# Revit family: Flopro Z2 Cuadrado
name_source: partatom
category: Luminarias
revit_build: Autodesk Revit 2015 (Build: 20140606_1530(x64)
units: mm (PartAtom-declared; Revit-internal decimal feet)

## types (4) — shared parameters
Anchura rectángulo de emisión = 72 mm  [stored 0.23622 ft]
Cambio de temperatura de color de luz atenuada = <Ninguno>
Fabricante = SECOM ILUMINACIÓN
Filtro de color = 16777215
Forma visible en renderización = No
Longitud de rectángulo de emisión = 72 mm  [stored 0.23622 ft]
Lámpara = LED Osram Duris
Ángulo de inclinación = 90.00°

## per-type parameters (varying)
| type | Archivo de red fotométrica | Comentarios de vataje | Descripción | Modelo | Óptica angulo de apertura |
| Flopro Z2 Cuadrado 6W / 48º | 6130 00 06 84 FLOPRO Z2 LED CUADRADO L48º 6W.IES | 6 W | 6130 00 06 84 | Flopro Z2 Cuadrado | 0.00° |
| Flopro Z2 Cuadrado 10W / 48º | 6130 00 10 84 FLOPRO Z2 LED CUADRADO L48º 6W.IES | 10W | 6130 00 10 84 | Flopro Z2 Cuadrado | 0.00° |
| Flopro Z2 Asimétrico cuadrado 7W / 11º | 6140 00 07 84 11 FLOPRO Z2 LED CUADRADO ASIMETRICO L11º 7W.IES | 7W | 6130 00 10 8411 | Flopro Z2 Asimétrico cuadrado | 11.00° |
| Flopro Z2 Asimétrico Cuadrado 7W / 48º | 6140 00 07 84 FLOPRO Z2 LED CUADRADO ASIMETRICO L48º 7W.IES | 7W | 6130 00 10 84 | Flopro Z2 Asimétrico cuadrado | 48.00° |

note: [stored X ft] marks values corroborated as IEEE doubles in the binary element streams (Revit-internal decimal feet)
